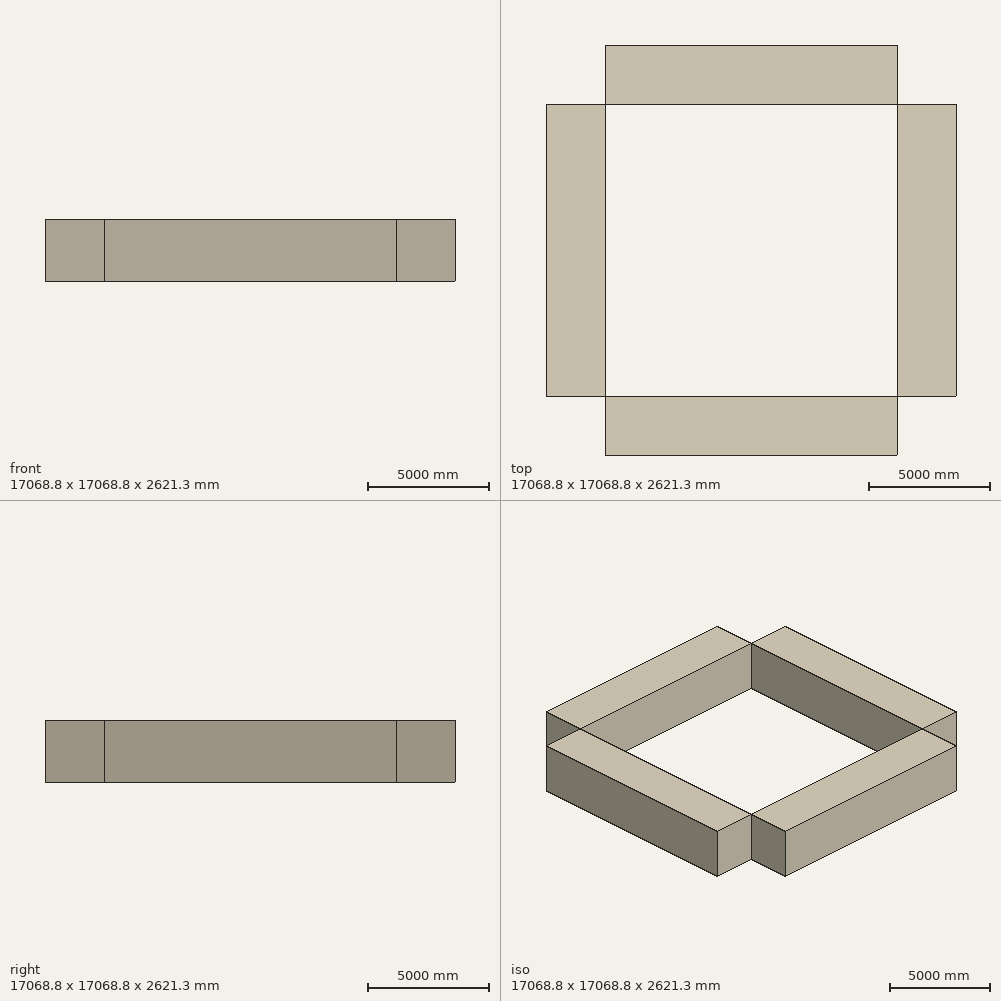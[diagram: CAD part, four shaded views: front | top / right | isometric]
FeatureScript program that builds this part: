
annotation { "Feature Type Name" : "Feature", "Feature Type Description" : "" }
export const myFeature = defineFeature(function(context is Context, id is Id, definition is map)
    precondition{}
    {
        {
            var Q0;
            Q0=qCreatedBy(makeId("Top.planeOp"),FACE);
            var sketch = newSketch(context, id + "F0", { "sketchPlane" : qUnion([Q0])});
            skLineSegment(sketch, "E0.bottom", {"start": v(-6096, 8534.4) * mm, "end": v(6096, 8534.4) * mm});
            skLineSegment(sketch, "E0.top", {"start": v(-6096, -8534.4) * mm, "end": v(6096, -8534.4) * mm});
            skLineSegment(sketch, "E0.left", {"start": v(-8534.4, 6096) * mm, "end": v(-8534.4, -6096) * mm});
            skLineSegment(sketch, "E0.right", {"start": v(8534.4, 6096) * mm, "end": v(8534.4, -6096) * mm});
            skPoint(sketch, "E0.middle", {"position": v(0, 0) * mm});
            skLineSegment(sketch, "E1.0", {"start": v(-8534.4, 6096) * mm, "end": v(0, 6096) * mm});
            skLineSegment(sketch, "E2.0", {"start": v(-6096, 8534.4) * mm, "end": v(-6096, 0) * mm});
            skLineSegment(sketch, "E3.0", {"start": v(-8534.4, -6096) * mm, "end": v(0, -6096) * mm});
            skLineSegment(sketch, "E4.0", {"start": v(6096, 8534.4) * mm, "end": v(6096, 0) * mm});
            skLineSegment(sketch, "E5", {"start": v(-6096, 0) * mm, "end": v(-6096, -8534.4) * mm});
            skLineSegment(sketch, "E6", {"start": v(0, 6096) * mm, "end": v(8534.4, 6096) * mm});
            skLineSegment(sketch, "E7", {"start": v(6096, 0) * mm, "end": v(6096, -8534.4) * mm});
            skLineSegment(sketch, "E8", {"start": v(0, -6096) * mm, "end": v(8534.4, -6096) * mm});
            skSolve(sketch);
        }
        {
            var Q0;
            {var subQ0=sQuery(id+"F0.wireOp",EDGE,"E0.top");Q0=makeQuery(id+"F0.imprint","IMPRINT",FACE,{"disambiguationData":[TD([[makeQuery(id+"F0.imprint","IMPRINT",EDGE,{"derivedFrom":subQ0}),1.0]])]});}
            var Q1;
            {var subQ0=sQuery(id+"F0.wireOp",EDGE,"E0.bottom");Q1=makeQuery(id+"F0.imprint","IMPRINT",FACE,{"disambiguationData":[TD([[makeQuery(id+"F0.imprint","IMPRINT",EDGE,{"derivedFrom":subQ0}),-1.0]])]});}
            var Q2;
            {var subQ0=sQuery(id+"F0.wireOp",EDGE,"E0.right");Q2=makeQuery(id+"F0.imprint","IMPRINT",FACE,{"disambiguationData":[TD([[makeQuery(id+"F0.imprint","IMPRINT",EDGE,{"derivedFrom":subQ0}),-1.0]])]});}
            var Q3;
            {var subQ0=sQuery(id+"F0.wireOp",EDGE,"E0.left");Q3=makeQuery(id+"F0.imprint","IMPRINT",FACE,{"disambiguationData":[TD([[makeQuery(id+"F0.imprint","IMPRINT",EDGE,{"derivedFrom":subQ0}),1.0]])]});}
            extrude(context, id + "F1", {"entities" : qUnion([Q0, Q1, Q2, Q3]), "depth" : 2621.28 * mm, "offsetDistance" : 30.48 * mm});
        }
    });
